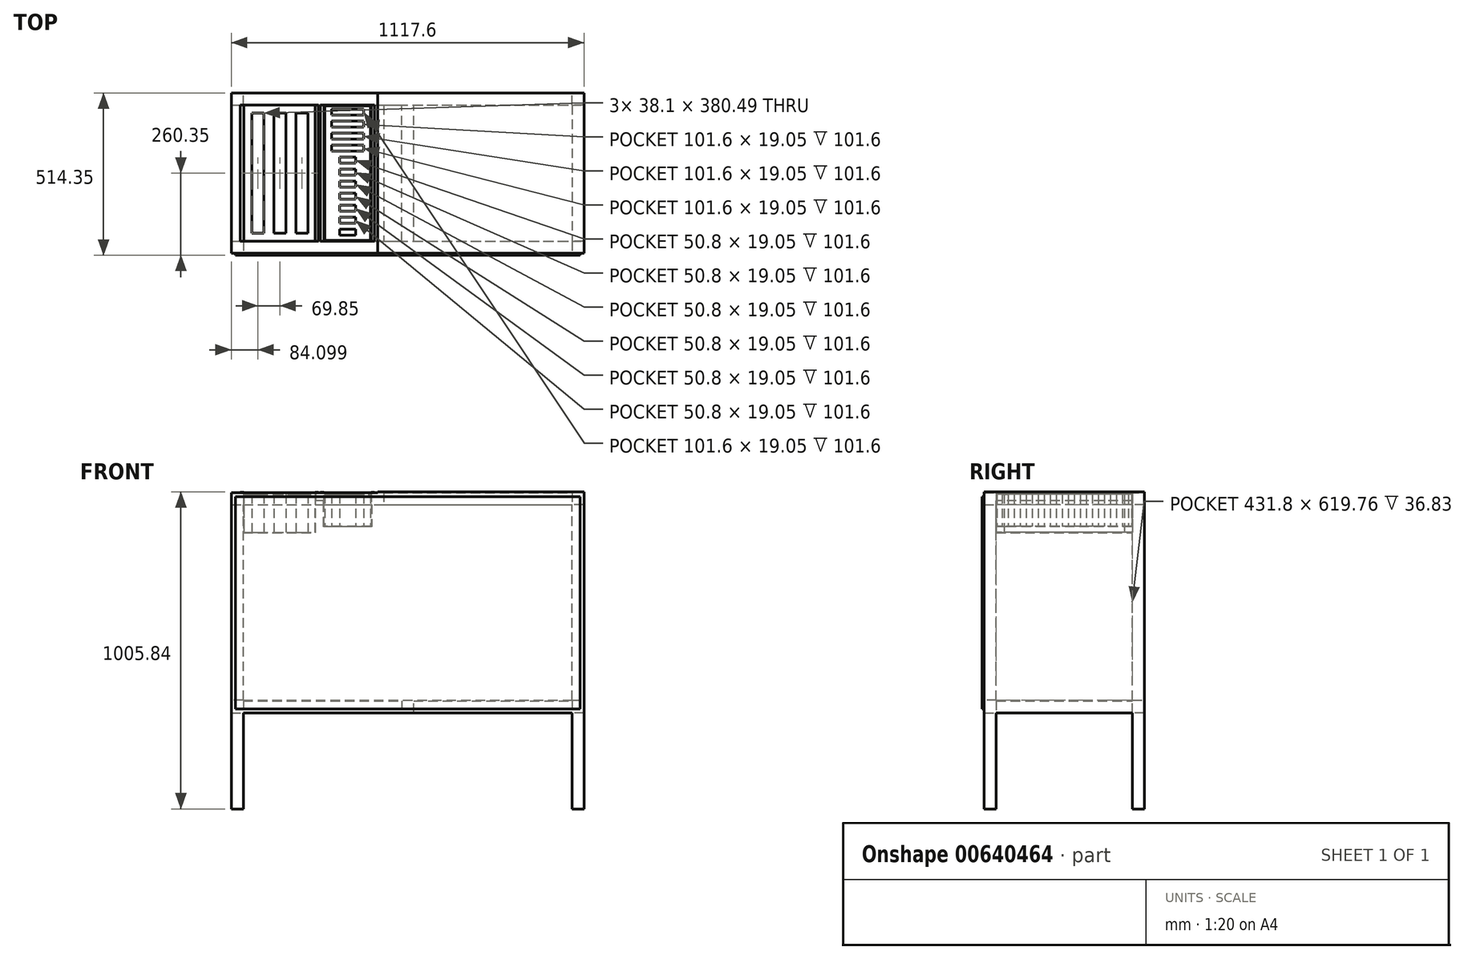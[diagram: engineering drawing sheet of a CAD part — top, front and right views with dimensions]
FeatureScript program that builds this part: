
annotation { "Feature Type Name" : "Feature", "Feature Type Description" : "" }
export const myFeature = defineFeature(function(context is Context, id is Id, definition is map)
    precondition{}
    {
        {
            var Q0;
            Q0=qCreatedBy(makeId("Top.planeOp"),FACE);
            var sketch = newSketch(context, id + "F0", { "sketchPlane" : qUnion([Q0])});
            skLineSegment(sketch, "E0.bottom", {"start": v(-558.8, 254) * mm, "end": v(558.8, 254) * mm});
            skLineSegment(sketch, "E0.top", {"start": v(-558.8, -254) * mm, "end": v(558.8, -254) * mm});
            skLineSegment(sketch, "E0.left", {"start": v(-558.8, 254) * mm, "end": v(-558.8, -254) * mm});
            skLineSegment(sketch, "E0.right", {"start": v(558.8, 254) * mm, "end": v(558.8, -254) * mm});
            skLineSegment(sketch, "E1", {"start": v(-558.8, -254) * mm, "end": v(558.8, 254) * mm, "construction": true});
            skLineSegment(sketch, "E2.0", {"start": v(-520.7, 215.9) * mm, "end": v(-520.7, -215.9) * mm});
            skLineSegment(sketch, "E2.1", {"start": v(-520.7, 215.9) * mm, "end": v(520.7, 215.9) * mm});
            skLineSegment(sketch, "E2.2", {"start": v(520.7, 215.9) * mm, "end": v(520.7, -215.9) * mm});
            skLineSegment(sketch, "E2.3", {"start": v(-520.7, -215.9) * mm, "end": v(520.7, -215.9) * mm});
            skSolve(sketch);
        }
        {
            var Q0;
            Q0 = qSketchRegion(id + "F0", true);
            extrude(context, id + "F1", {"entities" : qUnion([Q0]), "depth" : 38.1 * mm, "offsetDistance" : 25.4 * mm});
        }
        {
            var Q0;
            Q0=makeQuery(id+"F1.opExtrude","CAP_FACE",FACE,{"disambiguationData":[OSD([sQuery(id+"F0.wireOp",EDGE,"E0.bottom"),sQuery(id+"F0.wireOp",EDGE,"E0.top"),sQuery(id+"F0.wireOp",EDGE,"E0.left"),sQuery(id+"F0.wireOp",EDGE,"E0.right"),sQuery(id+"F0.wireOp",EDGE,"E2.0"),sQuery(id+"F0.wireOp",EDGE,"E2.1"),sQuery(id+"F0.wireOp",EDGE,"E2.2"),sQuery(id+"F0.wireOp",EDGE,"E2.3")])],"isStart":true});
            var sketch = newSketch(context, id + "F2", { "sketchPlane" : qUnion([Q0])});
            skLineSegment(sketch, "E3.bottom", {"start": v(-558.8, 254) * mm, "end": v(-520.7, 254) * mm});
            skLineSegment(sketch, "E3.top", {"start": v(-558.8, 215.9) * mm, "end": v(-520.7, 215.9) * mm});
            skLineSegment(sketch, "E3.left", {"start": v(-558.8, 254) * mm, "end": v(-558.8, 215.9) * mm});
            skLineSegment(sketch, "E3.right", {"start": v(-520.7, 254) * mm, "end": v(-520.7, 215.9) * mm});
            skLineSegment(sketch, "E4.bottom", {"start": v(558.8, 254) * mm, "end": v(520.7, 254) * mm});
            skLineSegment(sketch, "E4.top", {"start": v(558.8, 215.9) * mm, "end": v(520.7, 215.9) * mm});
            skLineSegment(sketch, "E4.left", {"start": v(558.8, 254) * mm, "end": v(558.8, 215.9) * mm});
            skLineSegment(sketch, "E4.right", {"start": v(520.7, 254) * mm, "end": v(520.7, 215.9) * mm});
            skLineSegment(sketch, "E5.bottom", {"start": v(558.8, -254) * mm, "end": v(520.7, -254) * mm});
            skLineSegment(sketch, "E5.top", {"start": v(558.8, -215.9) * mm, "end": v(520.7, -215.9) * mm});
            skLineSegment(sketch, "E5.left", {"start": v(558.8, -254) * mm, "end": v(558.8, -215.9) * mm});
            skLineSegment(sketch, "E5.right", {"start": v(520.7, -254) * mm, "end": v(520.7, -215.9) * mm});
            skLineSegment(sketch, "E6.bottom", {"start": v(-558.8, -254) * mm, "end": v(-520.7, -254) * mm});
            skLineSegment(sketch, "E6.top", {"start": v(-558.8, -215.9) * mm, "end": v(-520.7, -215.9) * mm});
            skLineSegment(sketch, "E6.left", {"start": v(-558.8, -254) * mm, "end": v(-558.8, -215.9) * mm});
            skLineSegment(sketch, "E6.right", {"start": v(-520.7, -254) * mm, "end": v(-520.7, -215.9) * mm});
            skSolve(sketch);
        }
        {
            var Q0;
            Q0 = qSketchRegion(id + "F2", true);
            extrude(context, id + "F3", {"entities" : qUnion([Q0]), "operationType" : NewBodyOperationType.ADD, "depth" : 965.2 * mm, "offsetDistance" : 25.4 * mm});
        }
        {
            var Q0;
            Q0=makeQuery(id+"F3.opExtrude","CAP_FACE",FACE,{"disambiguationData":[OSD([sQuery(id+"F2.wireOp",EDGE,"E3.bottom"),sQuery(id+"F2.wireOp",EDGE,"E3.top"),sQuery(id+"F2.wireOp",EDGE,"E3.left"),sQuery(id+"F2.wireOp",EDGE,"E3.right")])],"isStart":false});
            cPlane(context, id + "F4", {"entities" : qUnion([Q0]), "cplaneType" : CPlaneType.OFFSET, "offset" : 304.8 * mm, "oppositeDirection" : true, "width" : 152.4 * mm, "height" : 152.4 * mm});
        }
        {
            var Q0;
            Q0=qCreatedBy(id+"F4.planeOp",FACE);
            var sketch = newSketch(context, id + "F5", { "sketchPlane" : qUnion([Q0])});
            skLineSegment(sketch, "E7.bottom", {"start": v(-558.8, 254) * mm, "end": v(558.8, 254) * mm});
            skLineSegment(sketch, "E7.top", {"start": v(-558.8, -254) * mm, "end": v(558.8, -254) * mm});
            skLineSegment(sketch, "E7.left", {"start": v(-558.8, 254) * mm, "end": v(-558.8, -254) * mm});
            skLineSegment(sketch, "E7.right", {"start": v(558.8, 254) * mm, "end": v(558.8, -254) * mm});
            skLineSegment(sketch, "E8.bottom", {"start": v(-520.7, 215.9) * mm, "end": v(520.7, 215.9) * mm});
            skLineSegment(sketch, "E8.top", {"start": v(-520.7, -215.9) * mm, "end": v(520.7, -215.9) * mm});
            skLineSegment(sketch, "E8.left", {"start": v(-520.7, 215.9) * mm, "end": v(-520.7, -215.9) * mm});
            skLineSegment(sketch, "E8.right", {"start": v(520.7, 215.9) * mm, "end": v(520.7, -215.9) * mm});
            skSolve(sketch);
        }
        {
            var Q0;
            Q0 = qSketchRegion(id + "F5", true);
            extrude(context, id + "F6", {"entities" : qUnion([Q0]), "operationType" : NewBodyOperationType.ADD, "oppositeDirection" : true, "depth" : 38.1 * mm, "offsetDistance" : 25.4 * mm});
        }
        {
            var Q0;
            Q0=makeQuery(id+"F6.boolean.opBoolean","MERGE",FACE,{"derivedFrom":[makeQuery(id+"F3.boolean.opBoolean","MERGE",FACE,{"derivedFrom":[makeQuery(id+"F1.opExtrude","SWEPT_FACE",FACE,{"disambiguationData":[OSD([sQuery(id+"F0.wireOp",EDGE,"E0.left")])]}),makeQuery(id+"F3.opExtrude","SWEPT_FACE",FACE,{"disambiguationData":[OSD([sQuery(id+"F2.wireOp",EDGE,"E3.left")])]}),makeQuery(id+"F3.opExtrude","SWEPT_FACE",FACE,{"disambiguationData":[OSD([sQuery(id+"F2.wireOp",EDGE,"E6.left")])]})]}),makeQuery(id+"F6.opExtrude","SWEPT_FACE",FACE,{"disambiguationData":[OSD([sQuery(id+"F5.wireOp",EDGE,"E7.left")])]})]});
            var sketch = newSketch(context, id + "F7", { "sketchPlane" : qUnion([Q0])});
            skLineSegment(sketch, "E9.0", {"start": v(-215.9, -622.3) * mm, "end": v(-215.9, 0) * mm});
            skLineSegment(sketch, "E10.0", {"start": v(-215.9, 0) * mm, "end": v(215.9, 0) * mm});
            skLineSegment(sketch, "E11.0", {"start": v(215.9, -622.3) * mm, "end": v(215.9, 0) * mm});
            skLineSegment(sketch, "E11.1", {"start": v(215.9, -622.3) * mm, "end": v(-215.9, -622.3) * mm});
            skSolve(sketch);
        }
        {
            var Q0;
            Q0 = qSketchRegion(id + "F7", true);
            extrude(context, id + "F8", {"entities" : qUnion([Q0]), "operationType" : NewBodyOperationType.ADD, "oppositeDirection" : true, "depth" : 1.27 * mm, "offsetDistance" : 25.4 * mm});
        }
        {
            var Q0;
            Q0=makeQuery(id+"F6.boolean.opBoolean","MERGE",FACE,{"derivedFrom":[makeQuery(id+"F3.boolean.opBoolean","MERGE",FACE,{"derivedFrom":[makeQuery(id+"F1.opExtrude","SWEPT_FACE",FACE,{"disambiguationData":[OSD([sQuery(id+"F0.wireOp",EDGE,"E0.right")])]}),makeQuery(id+"F3.opExtrude","SWEPT_FACE",FACE,{"disambiguationData":[OSD([sQuery(id+"F2.wireOp",EDGE,"E4.left")])]}),makeQuery(id+"F3.opExtrude","SWEPT_FACE",FACE,{"disambiguationData":[OSD([sQuery(id+"F2.wireOp",EDGE,"E5.left")])]})]}),makeQuery(id+"F6.opExtrude","SWEPT_FACE",FACE,{"disambiguationData":[OSD([sQuery(id+"F5.wireOp",EDGE,"E7.right")])]})]});
            var sketch = newSketch(context, id + "F9", { "sketchPlane" : qUnion([Q0])});
            skLineSegment(sketch, "E12.0", {"start": v(215.9, 0) * mm, "end": v(-215.9, 0) * mm});
            skLineSegment(sketch, "E12.1", {"start": v(-215.9, -622.3) * mm, "end": v(-215.9, 0) * mm});
            skLineSegment(sketch, "E12.2", {"start": v(215.9, -622.3) * mm, "end": v(215.9, 0) * mm});
            skLineSegment(sketch, "E12.3", {"start": v(-215.9, -622.3) * mm, "end": v(215.9, -622.3) * mm});
            skSolve(sketch);
        }
        {
            var Q0;
            Q0 = qSketchRegion(id + "F9", true);
            extrude(context, id + "F10", {"entities" : qUnion([Q0]), "operationType" : NewBodyOperationType.ADD, "oppositeDirection" : true, "depth" : 1.27 * mm, "offsetDistance" : 25.4 * mm});
        }
        {
            var Q0;
            Q0=makeQuery(id+"F1.opExtrude","SWEPT_FACE",FACE,{"disambiguationData":[OSD([sQuery(id+"F0.wireOp",EDGE,"E2.3")])]});
            var sketch = newSketch(context, id + "F11", { "sketchPlane" : qUnion([Q0])});
            skLineSegment(sketch, "E13.bottom", {"start": v(76.2, 38.1) * mm, "end": v(114.3, 38.1) * mm});
            skLineSegment(sketch, "E13.top", {"start": v(76.2, 0) * mm, "end": v(114.3, 0) * mm});
            skLineSegment(sketch, "E13.left", {"start": v(76.2, 38.1) * mm, "end": v(76.2, 0) * mm});
            skLineSegment(sketch, "E13.right", {"start": v(114.3, 38.1) * mm, "end": v(114.3, 0) * mm});
            skLineSegment(sketch, "E14.bottom", {"start": v(266.7, 38.1) * mm, "end": v(292.1, 38.1) * mm});
            skLineSegment(sketch, "E14.top", {"start": v(266.7, 12.7) * mm, "end": v(292.1, 12.7) * mm});
            skLineSegment(sketch, "E14.left", {"start": v(266.7, 38.1) * mm, "end": v(266.7, 12.7) * mm});
            skLineSegment(sketch, "E14.right", {"start": v(292.1, 38.1) * mm, "end": v(292.1, 12.7) * mm});
            skSolve(sketch);
        }
        {
            var Q0;
            Q0 = qSketchRegion(id + "F11", true);
            var Q1;
            Q1=makeQuery(id+"F1.opExtrude","SWEPT_FACE",FACE,{"disambiguationData":[OSD([sQuery(id+"F0.wireOp",EDGE,"E2.1")])]});
            extrude(context, id + "F12", {"entities" : qUnion([Q0]), "operationType" : NewBodyOperationType.ADD, "endBound" : BoundingType.UP_TO_SURFACE, "depth" : 25.4 * mm, "endBoundEntityFace" : qUnion([Q1]), "offsetDistance" : 25.4 * mm});
        }
        {
            var Q0;
            Q0=makeQuery(id+"F12.boolean.opBoolean","MERGE",FACE,{"derivedFrom":[makeQuery(id+"F1.opExtrude","CAP_FACE",FACE,{"disambiguationData":[OSD([sQuery(id+"F0.wireOp",EDGE,"E0.bottom"),sQuery(id+"F0.wireOp",EDGE,"E0.top"),sQuery(id+"F0.wireOp",EDGE,"E0.left"),sQuery(id+"F0.wireOp",EDGE,"E0.right"),sQuery(id+"F0.wireOp",EDGE,"E2.0"),sQuery(id+"F0.wireOp",EDGE,"E2.1"),sQuery(id+"F0.wireOp",EDGE,"E2.2"),sQuery(id+"F0.wireOp",EDGE,"E2.3")])],"isStart":false}),makeQuery(id+"F12.opExtrude","SWEPT_FACE",FACE,{"disambiguationData":[OSD([sQuery(id+"F11.wireOp",EDGE,"E13.bottom")])]}),makeQuery(id+"F12.opExtrude","SWEPT_FACE",FACE,{"disambiguationData":[OSD([sQuery(id+"F11.wireOp",EDGE,"E14.bottom")])]})]});
            var sketch = newSketch(context, id + "F13", { "sketchPlane" : qUnion([Q0])});
            skLineSegment(sketch, "E15.0", {"start": v(558.8, 254) * mm, "end": v(558.8, -254) * mm});
            skLineSegment(sketch, "E16", {"start": v(558.8, -254) * mm, "end": v(-95.25, -254) * mm});
            skLineSegment(sketch, "E17", {"start": v(-95.25, -254) * mm, "end": v(-95.25, 254) * mm});
            skLineSegment(sketch, "E18", {"start": v(-95.25, 254) * mm, "end": v(558.8, 254) * mm});
            skSolve(sketch);
        }
        {
            var Q0;
            Q0 = qSketchRegion(id + "F13", true);
            extrude(context, id + "F14", {"entities" : qUnion([Q0]), "operationType" : NewBodyOperationType.ADD, "depth" : 2.54 * mm, "offsetDistance" : 25.4 * mm});
        }
        {
            var Q0;
            {var subQ0=sQuery(id+"F0.wireOp",EDGE,"E2.3");var subQ3=sQuery(id+"F0.wireOp",EDGE,"E2.0");Q0=makeQuery(id+"F12.boolean.opBoolean","SPLIT",FACE,{"disambiguationData":[TD([makeQuery(id+"F1.opExtrude","SWEPT_FACE",FACE,{"disambiguationData":[OSD([subQ3])]})])],"derivedFrom":makeQuery(id+"F1.opExtrude","SWEPT_FACE",FACE,{"disambiguationData":[OSD([subQ0])]})});}
            var sketch = newSketch(context, id + "F15", { "sketchPlane" : qUnion([Q0])});
            skLineSegment(sketch, "E19", {"start": v(104.77, 38.1) * mm, "end": v(114.3, 38.1) * mm});
            skLineSegment(sketch, "E20", {"start": v(114.3, 38.1) * mm, "end": v(114.3, -69.85) * mm});
            skLineSegment(sketch, "E21", {"start": v(114.3, -69.85) * mm, "end": v(266.7, -69.85) * mm});
            skLineSegment(sketch, "E22", {"start": v(266.7, -69.85) * mm, "end": v(266.7, 38.1) * mm});
            skLineSegment(sketch, "E23", {"start": v(266.7, 38.1) * mm, "end": v(276.23, 38.1) * mm});
            skLineSegment(sketch, "E24.0", {"start": v(265.43, 39.37) * mm, "end": v(276.23, 39.37) * mm});
            skLineSegment(sketch, "E24.1", {"start": v(104.77, 39.37) * mm, "end": v(115.57, 39.37) * mm});
            skLineSegment(sketch, "E24.2", {"start": v(115.57, 39.37) * mm, "end": v(115.57, -68.58) * mm});
            skLineSegment(sketch, "E24.3", {"start": v(115.57, -68.58) * mm, "end": v(265.43, -68.58) * mm});
            skLineSegment(sketch, "E24.4", {"start": v(265.43, -68.58) * mm, "end": v(265.43, 39.37) * mm});
            skLineSegment(sketch, "E25", {"start": v(104.77, 39.37) * mm, "end": v(104.77, 38.1) * mm});
            skLineSegment(sketch, "E26", {"start": v(276.23, 39.37) * mm, "end": v(276.23, 38.1) * mm});
            skSolve(sketch);
        }
        {
            var Q0;
            Q0 = qSketchRegion(id + "F15", true);
            var Q1;
            {var subQ2=sQuery(id+"F0.wireOp",EDGE,"E2.1");var subQ3=sQuery(id+"F0.wireOp",EDGE,"E2.0");Q1=makeQuery(id+"F12.boolean.opBoolean","SPLIT",FACE,{"disambiguationData":[TD([makeQuery(id+"F1.opExtrude","SWEPT_FACE",FACE,{"disambiguationData":[OSD([subQ3])]})])],"derivedFrom":makeQuery(id+"F1.opExtrude","SWEPT_FACE",FACE,{"disambiguationData":[OSD([subQ2])]})});}
            extrude(context, id + "F16", {"entities" : qUnion([Q0]), "operationType" : NewBodyOperationType.ADD, "endBound" : BoundingType.UP_TO_SURFACE, "depth" : 25.4 * mm, "endBoundEntityFace" : qUnion([Q1]), "offsetDistance" : 25.4 * mm});
        }
        {
            var Q0;
            Q0=makeQuery(id+"F16.opExtrude","SWEPT_FACE",FACE,{"disambiguationData":[OSD([sQuery(id+"F15.wireOp",EDGE,"E24.3")])]});
            var sketch = newSketch(context, id + "F17", { "sketchPlane" : qUnion([Q0])});
            skLineSegment(sketch, "E27.bottom", {"start": v(-241.3, 165.1) * mm, "end": v(-139.7, 165.1) * mm});
            skLineSegment(sketch, "E27.top", {"start": v(-241.3, 146.05) * mm, "end": v(-139.7, 146.05) * mm});
            skLineSegment(sketch, "E27.left", {"start": v(-241.3, 165.1) * mm, "end": v(-241.3, 146.05) * mm});
            skLineSegment(sketch, "E27.right", {"start": v(-139.7, 165.1) * mm, "end": v(-139.7, 146.05) * mm});
            skLineSegment(sketch, "E28.bottom", {"start": v(-241.3, 127) * mm, "end": v(-139.7, 127) * mm});
            skLineSegment(sketch, "E28.top", {"start": v(-241.3, 107.95) * mm, "end": v(-139.7, 107.95) * mm});
            skLineSegment(sketch, "E28.left", {"start": v(-241.3, 127) * mm, "end": v(-241.3, 107.95) * mm});
            skLineSegment(sketch, "E28.right", {"start": v(-139.7, 127) * mm, "end": v(-139.7, 107.95) * mm});
            skLineSegment(sketch, "E29.bottom", {"start": v(-241.3, 88.9) * mm, "end": v(-139.7, 88.9) * mm});
            skLineSegment(sketch, "E29.top", {"start": v(-241.3, 69.85) * mm, "end": v(-139.7, 69.85) * mm});
            skLineSegment(sketch, "E29.left", {"start": v(-241.3, 88.9) * mm, "end": v(-241.3, 69.85) * mm});
            skLineSegment(sketch, "E29.right", {"start": v(-139.7, 88.9) * mm, "end": v(-139.7, 69.85) * mm});
            skLineSegment(sketch, "E30.bottom", {"start": v(-215.9, 50.8) * mm, "end": v(-165.1, 50.8) * mm});
            skLineSegment(sketch, "E30.top", {"start": v(-215.9, 31.75) * mm, "end": v(-165.1, 31.75) * mm});
            skLineSegment(sketch, "E30.left", {"start": v(-215.9, 50.8) * mm, "end": v(-215.9, 31.75) * mm});
            skLineSegment(sketch, "E30.right", {"start": v(-165.1, 50.8) * mm, "end": v(-165.1, 31.75) * mm});
            skLineSegment(sketch, "E31.bottom", {"start": v(-215.9, 12.7) * mm, "end": v(-165.1, 12.7) * mm});
            skLineSegment(sketch, "E31.top", {"start": v(-215.9, -6.35) * mm, "end": v(-165.1, -6.35) * mm});
            skLineSegment(sketch, "E31.left", {"start": v(-215.9, 12.7) * mm, "end": v(-215.9, -6.35) * mm});
            skLineSegment(sketch, "E31.right", {"start": v(-165.1, 12.7) * mm, "end": v(-165.1, -6.35) * mm});
            skLineSegment(sketch, "E32.bottom", {"start": v(-215.9, -25.4) * mm, "end": v(-165.1, -25.4) * mm});
            skLineSegment(sketch, "E32.top", {"start": v(-215.9, -44.45) * mm, "end": v(-165.1, -44.45) * mm});
            skLineSegment(sketch, "E32.left", {"start": v(-215.9, -25.4) * mm, "end": v(-215.9, -44.45) * mm});
            skLineSegment(sketch, "E32.right", {"start": v(-165.1, -25.4) * mm, "end": v(-165.1, -44.45) * mm});
            skLineSegment(sketch, "E33.bottom", {"start": v(-215.9, -63.5) * mm, "end": v(-165.1, -63.5) * mm});
            skLineSegment(sketch, "E33.top", {"start": v(-215.9, -82.55) * mm, "end": v(-165.1, -82.55) * mm});
            skLineSegment(sketch, "E33.left", {"start": v(-215.9, -63.5) * mm, "end": v(-215.9, -82.55) * mm});
            skLineSegment(sketch, "E33.right", {"start": v(-165.1, -63.5) * mm, "end": v(-165.1, -82.55) * mm});
            skLineSegment(sketch, "E34.bottom", {"start": v(-215.9, -101.6) * mm, "end": v(-165.1, -101.6) * mm});
            skLineSegment(sketch, "E34.top", {"start": v(-215.9, -120.65) * mm, "end": v(-165.1, -120.65) * mm});
            skLineSegment(sketch, "E34.left", {"start": v(-215.9, -101.6) * mm, "end": v(-215.9, -120.65) * mm});
            skLineSegment(sketch, "E34.right", {"start": v(-165.1, -101.6) * mm, "end": v(-165.1, -120.65) * mm});
            skLineSegment(sketch, "E35.bottom", {"start": v(-215.9, -139.7) * mm, "end": v(-165.1, -139.7) * mm});
            skLineSegment(sketch, "E35.top", {"start": v(-215.9, -158.75) * mm, "end": v(-165.1, -158.75) * mm});
            skLineSegment(sketch, "E35.left", {"start": v(-215.9, -139.7) * mm, "end": v(-215.9, -158.75) * mm});
            skLineSegment(sketch, "E35.right", {"start": v(-165.1, -139.7) * mm, "end": v(-165.1, -158.75) * mm});
            skLineSegment(sketch, "E36.bottom", {"start": v(-215.9, -196.85) * mm, "end": v(-165.1, -196.85) * mm});
            skLineSegment(sketch, "E36.top", {"start": v(-215.9, -177.8) * mm, "end": v(-165.1, -177.8) * mm});
            skLineSegment(sketch, "E36.left", {"start": v(-215.9, -196.85) * mm, "end": v(-215.9, -177.8) * mm});
            skLineSegment(sketch, "E36.right", {"start": v(-165.1, -196.85) * mm, "end": v(-165.1, -177.8) * mm});
            skLineSegment(sketch, "E37.bottom", {"start": v(-241.3, 203.2) * mm, "end": v(-139.7, 203.2) * mm});
            skLineSegment(sketch, "E37.top", {"start": v(-241.3, 184.15) * mm, "end": v(-139.7, 184.15) * mm});
            skLineSegment(sketch, "E37.left", {"start": v(-241.3, 203.2) * mm, "end": v(-241.3, 184.15) * mm});
            skLineSegment(sketch, "E37.right", {"start": v(-139.7, 203.2) * mm, "end": v(-139.7, 184.15) * mm});
            skLineSegment(sketch, "E38", {"start": v(-190.5, -215.9) * mm, "end": v(-190.5, 215.9) * mm, "construction": true});
            skLineSegment(sketch, "E39.0", {"start": v(-262.9, 213.36) * mm, "end": v(-118.1, 213.36) * mm});
            skLineSegment(sketch, "E39.1", {"start": v(-262.9, 213.36) * mm, "end": v(-262.9, -213.36) * mm});
            skLineSegment(sketch, "E39.2", {"start": v(-262.9, -213.36) * mm, "end": v(-118.1, -213.36) * mm});
            skLineSegment(sketch, "E39.3", {"start": v(-118.1, 213.36) * mm, "end": v(-118.1, -213.36) * mm});
            skSolve(sketch);
        }
        {
            var Q0;
            Q0 = qSketchRegion(id + "F17", true);
            extrude(context, id + "F18", {"entities" : qUnion([Q0]), "operationType" : NewBodyOperationType.ADD, "depth" : 101.6 * mm, "offsetDistance" : 25.4 * mm});
        }
        {
            var Q0;
            {var subQ0=sQuery(id+"F5.wireOp",EDGE,"E8.top");var subQ1=sQuery(id+"F5.wireOp",EDGE,"E8.right");var subQ2=sQuery(id+"F5.wireOp",EDGE,"E8.left");var subQ3=sQuery(id+"F5.wireOp",EDGE,"E7.top");var subQ4=makeQuery(id+"F6.opExtrude","CAP_FACE",FACE,{"disambiguationData":[OSD([sQuery(id+"F5.wireOp",EDGE,"E7.bottom"),subQ3,sQuery(id+"F5.wireOp",EDGE,"E7.left"),sQuery(id+"F5.wireOp",EDGE,"E7.right"),sQuery(id+"F5.wireOp",EDGE,"E8.bottom"),subQ0,subQ2,subQ1])],"isStart":false});Q0=makeQuery(id+"F6.boolean.opBoolean","SPLIT",FACE,{"disambiguationData":[TD([makeQuery(id+"F1.opExtrude","SWEPT_FACE",FACE,{"disambiguationData":[OSD([sQuery(id+"F0.wireOp",EDGE,"E0.bottom")])]})])],"derivedFrom":subQ4});}
            var sketch = newSketch(context, id + "F19", { "sketchPlane" : qUnion([Q0])});
            skLineSegment(sketch, "E40.bottom", {"start": v(-558.8, 254) * mm, "end": v(558.8, 254) * mm});
            skLineSegment(sketch, "E40.top", {"start": v(-558.8, -254) * mm, "end": v(558.8, -254) * mm});
            skLineSegment(sketch, "E40.left", {"start": v(-558.8, 254) * mm, "end": v(-558.8, -254) * mm});
            skLineSegment(sketch, "E40.right", {"start": v(558.8, 254) * mm, "end": v(558.8, -254) * mm});
            skSolve(sketch);
        }
        {
            var Q0;
            Q0 = qSketchRegion(id + "F19", true);
            extrude(context, id + "F20", {"entities" : qUnion([Q0]), "operationType" : NewBodyOperationType.ADD, "depth" : 2.54 * mm, "offsetDistance" : 25.4 * mm});
        }
        {
            var Q0;
            Q0=makeQuery(id+"F6.opExtrude","SWEPT_FACE",FACE,{"disambiguationData":[OSD([sQuery(id+"F5.wireOp",EDGE,"E8.top")])]});
            var sketch = newSketch(context, id + "F21", { "sketchPlane" : qUnion([Q0])});
            skLineSegment(sketch, "E41.bottom", {"start": v(-19.05, -660.4) * mm, "end": v(19.05, -660.4) * mm});
            skLineSegment(sketch, "E41.top", {"start": v(-19.05, -622.3) * mm, "end": v(19.05, -622.3) * mm});
            skLineSegment(sketch, "E41.left", {"start": v(-19.05, -660.4) * mm, "end": v(-19.05, -622.3) * mm});
            skLineSegment(sketch, "E41.right", {"start": v(19.05, -660.4) * mm, "end": v(19.05, -622.3) * mm});
            skSolve(sketch);
        }
        {
            var Q0;
            Q0 = qSketchRegion(id + "F21", true);
            var Q1;
            Q1=makeQuery(id+"F6.opExtrude","SWEPT_FACE",FACE,{"disambiguationData":[OSD([sQuery(id+"F5.wireOp",EDGE,"E8.bottom")])]});
            extrude(context, id + "F22", {"entities" : qUnion([Q0]), "operationType" : NewBodyOperationType.ADD, "endBound" : BoundingType.UP_TO_SURFACE, "depth" : 25.4 * mm, "endBoundEntityFace" : qUnion([Q1]), "offsetDistance" : 25.4 * mm});
        }
        {
            var Q0;
            Q0=makeQuery(id+"F20.boolean.opBoolean","MERGE",FACE,{"derivedFrom":[makeQuery(id+"F14.boolean.opBoolean","MERGE",FACE,{"derivedFrom":[makeQuery(id+"F6.boolean.opBoolean","MERGE",FACE,{"derivedFrom":[makeQuery(id+"F3.boolean.opBoolean","MERGE",FACE,{"derivedFrom":[makeQuery(id+"F1.opExtrude","SWEPT_FACE",FACE,{"disambiguationData":[OSD([sQuery(id+"F0.wireOp",EDGE,"E0.top")])]}),makeQuery(id+"F3.opExtrude","SWEPT_FACE",FACE,{"disambiguationData":[OSD([sQuery(id+"F2.wireOp",EDGE,"E3.bottom")])]}),makeQuery(id+"F3.opExtrude","SWEPT_FACE",FACE,{"disambiguationData":[OSD([sQuery(id+"F2.wireOp",EDGE,"E4.bottom")])]})]}),makeQuery(id+"F6.opExtrude","SWEPT_FACE",FACE,{"disambiguationData":[OSD([sQuery(id+"F5.wireOp",EDGE,"E7.bottom")])]})]}),makeQuery(id+"F14.opExtrude","SWEPT_FACE",FACE,{"disambiguationData":[OSD([sQuery(id+"F13.wireOp",EDGE,"E16")])]})]}),makeQuery(id+"F20.opExtrude","SWEPT_FACE",FACE,{"disambiguationData":[OSD([sQuery(id+"F19.wireOp",EDGE,"E40.top")])]})]});
            var sketch = newSketch(context, id + "F23", { "sketchPlane" : qUnion([Q0])});
            skLineSegment(sketch, "E42.bottom", {"start": v(-546.1, 25.4) * mm, "end": v(546.1, 25.4) * mm});
            skLineSegment(sketch, "E42.top", {"start": v(-546.1, -647.7) * mm, "end": v(546.1, -647.7) * mm});
            skLineSegment(sketch, "E42.left", {"start": v(-546.1, 25.4) * mm, "end": v(-546.1, -647.7) * mm});
            skLineSegment(sketch, "E42.right", {"start": v(546.1, 25.4) * mm, "end": v(546.1, -647.7) * mm});
            skSolve(sketch);
        }
        {
            var Q0;
            Q0 = qSketchRegion(id + "F23", true);
            extrude(context, id + "F24", {"entities" : qUnion([Q0]), "operationType" : NewBodyOperationType.ADD, "depth" : 6.35 * mm, "offsetDistance" : 25.4 * mm});
        }
        {
            var Q0;
            {var subQ4=sQuery(id+"F0.wireOp",EDGE,"E2.1");var subQ5=sQuery(id+"F0.wireOp",EDGE,"E2.0");var subQ15=makeQuery(id+"F1.opExtrude","SWEPT_FACE",FACE,{"disambiguationData":[OSD([subQ5])]});Q0=makeQuery(id+"F16.boolean.opBoolean","SPLIT",FACE,{"disambiguationData":[TD([subQ15])],"derivedFrom":makeQuery(id+"F12.boolean.opBoolean","SPLIT",FACE,{"disambiguationData":[TD([subQ15])],"derivedFrom":makeQuery(id+"F1.opExtrude","SWEPT_FACE",FACE,{"disambiguationData":[OSD([subQ4])]})})});}
            var sketch = newSketch(context, id + "F25", { "sketchPlane" : qUnion([Q0])});
            skSolve(sketch);
        }
        {
            var Q0;
            {var subQ0=sQuery(id+"F0.wireOp",EDGE,"E2.0");var subQ2=sQuery(id+"F0.wireOp",EDGE,"E2.1");Q0=makeQuery(id+"F25.imprint","IMPRINT",FACE,{"disambiguationData":[TD([[makeQuery(id+"F25.imprint","IMPRINT",EDGE,{"derivedFrom":makeQuery(id+"F1.opExtrude","SWEPT_EDGE",EDGE,{"disambiguationData":[OSD([subQ0,subQ2])]})}),1.0]])]});}
            var sketch = newSketch(context, id + "F26", { "sketchPlane" : qUnion([Q0])});
            skLineSegment(sketch, "E43", {"start": v(-530.2, 38.13) * mm, "end": v(-520.67, 38.13) * mm});
            skLineSegment(sketch, "E44", {"start": v(-520.67, 38.13) * mm, "end": v(-520.67, -88.87) * mm});
            skLineSegment(sketch, "E45", {"start": v(-520.67, -88.87) * mm, "end": v(-292.13, -88.87) * mm});
            skLineSegment(sketch, "E46", {"start": v(-292.13, -88.87) * mm, "end": v(-292.13, 38.13) * mm});
            skLineSegment(sketch, "E47", {"start": v(-292.13, 38.13) * mm, "end": v(-282.6, 38.13) * mm});
            skLineSegment(sketch, "E48.0", {"start": v(-293.4, 39.4) * mm, "end": v(-282.6, 39.4) * mm});
            skLineSegment(sketch, "E48.1", {"start": v(-530.2, 39.4) * mm, "end": v(-519.4, 39.4) * mm});
            skLineSegment(sketch, "E48.2", {"start": v(-519.4, 39.4) * mm, "end": v(-519.4, -87.6) * mm});
            skLineSegment(sketch, "E48.3", {"start": v(-519.4, -87.6) * mm, "end": v(-293.4, -87.6) * mm});
            skLineSegment(sketch, "E48.4", {"start": v(-293.4, -87.6) * mm, "end": v(-293.4, 39.4) * mm});
            skLineSegment(sketch, "E49", {"start": v(-282.6, 39.4) * mm, "end": v(-282.6, 38.13) * mm});
            skLineSegment(sketch, "E50", {"start": v(-530.2, 39.4) * mm, "end": v(-530.2, 38.13) * mm});
            skSolve(sketch);
        }
        {
            var Q0;
            Q0 = qSketchRegion(id + "F26", true);
            var Q1;
            {var subQ2=sQuery(id+"F0.wireOp",EDGE,"E2.3");var subQ5=sQuery(id+"F0.wireOp",EDGE,"E2.0");var subQ15=makeQuery(id+"F1.opExtrude","SWEPT_FACE",FACE,{"disambiguationData":[OSD([subQ5])]});Q1=makeQuery(id+"F16.boolean.opBoolean","SPLIT",FACE,{"disambiguationData":[TD([subQ15])],"derivedFrom":makeQuery(id+"F12.boolean.opBoolean","SPLIT",FACE,{"disambiguationData":[TD([subQ15])],"derivedFrom":makeQuery(id+"F1.opExtrude","SWEPT_FACE",FACE,{"disambiguationData":[OSD([subQ2])]})})});}
            extrude(context, id + "F27", {"entities" : qUnion([Q0]), "operationType" : NewBodyOperationType.ADD, "endBound" : BoundingType.UP_TO_SURFACE, "depth" : 25.4 * mm, "endBoundEntityFace" : qUnion([Q1]), "offsetDistance" : 25.4 * mm});
        }
        {
            var Q0;
            Q0=makeQuery(id+"F27.opExtrude","SWEPT_FACE",FACE,{"disambiguationData":[OSD([sQuery(id+"F26.wireOp",EDGE,"E48.3")])]});
            cPlane(context, id + "F28", {"entities" : qUnion([Q0]), "cplaneType" : CPlaneType.OFFSET, "offset" : 0.03 * mm, "width" : 152.4 * mm, "height" : 152.4 * mm});
        }
        {
            var Q0;
            Q0=qCreatedBy(id+"F28.planeOp",FACE);
            var sketch = newSketch(context, id + "F29", { "sketchPlane" : qUnion([Q0])});
            skLineSegment(sketch, "E51.bottom", {"start": v(-519.15, 215.65) * mm, "end": v(-293.65, 215.65) * mm});
            skLineSegment(sketch, "E51.top", {"start": v(-519.15, -215.65) * mm, "end": v(-293.65, -215.65) * mm});
            skLineSegment(sketch, "E51.left", {"start": v(-519.15, 215.65) * mm, "end": v(-519.15, -215.65) * mm});
            skLineSegment(sketch, "E51.right", {"start": v(-293.65, 215.65) * mm, "end": v(-293.65, -215.65) * mm});
            skLineSegment(sketch, "E52.bottom", {"start": v(-493.75, 190.25) * mm, "end": v(-455.65, 190.25) * mm});
            skLineSegment(sketch, "E52.top", {"start": v(-493.75, -190.25) * mm, "end": v(-455.65, -190.25) * mm});
            skLineSegment(sketch, "E52.left", {"start": v(-493.75, 190.25) * mm, "end": v(-493.75, -190.25) * mm});
            skLineSegment(sketch, "E52.right", {"start": v(-455.65, 190.25) * mm, "end": v(-455.65, -190.25) * mm});
            skPoint(sketch, "E53.firstSnap0", {"position": v(-474.7, 190.25) * mm});
            skLineSegment(sketch, "E53.bottom", {"start": v(-354.05, 190.25) * mm, "end": v(-315.95, 190.25) * mm});
            skLineSegment(sketch, "E53.top", {"start": v(-354.05, -190.25) * mm, "end": v(-315.95, -190.25) * mm});
            skLineSegment(sketch, "E53.left", {"start": v(-354.05, 190.25) * mm, "end": v(-354.05, -190.25) * mm});
            skLineSegment(sketch, "E53.right", {"start": v(-315.95, 190.25) * mm, "end": v(-315.95, -190.25) * mm});
            skLineSegment(sketch, "E54.bottom", {"start": v(-423.9, 190.25) * mm, "end": v(-385.8, 190.25) * mm});
            skLineSegment(sketch, "E54.top", {"start": v(-423.9, -190.25) * mm, "end": v(-385.8, -190.25) * mm});
            skLineSegment(sketch, "E54.left", {"start": v(-423.9, 190.25) * mm, "end": v(-423.9, -190.25) * mm});
            skLineSegment(sketch, "E54.right", {"start": v(-385.8, 190.25) * mm, "end": v(-385.8, -190.25) * mm});
            skSolve(sketch);
        }
        {
            var Q0;
            Q0 = qSketchRegion(id + "F29", true);
            var Q1;
            Q1=makeQuery(id+"F18.opExtrude","CAP_FACE",FACE,{"disambiguationData":[OSD([sQuery(id+"F17.wireOp",EDGE,"E27.bottom"),sQuery(id+"F17.wireOp",EDGE,"E27.top"),sQuery(id+"F17.wireOp",EDGE,"E27.left"),sQuery(id+"F17.wireOp",EDGE,"E27.right"),sQuery(id+"F17.wireOp",EDGE,"E28.bottom"),sQuery(id+"F17.wireOp",EDGE,"E28.top"),sQuery(id+"F17.wireOp",EDGE,"E28.left"),sQuery(id+"F17.wireOp",EDGE,"E28.right"),sQuery(id+"F17.wireOp",EDGE,"E29.bottom"),sQuery(id+"F17.wireOp",EDGE,"E29.top"),sQuery(id+"F17.wireOp",EDGE,"E29.left"),sQuery(id+"F17.wireOp",EDGE,"E29.right"),sQuery(id+"F17.wireOp",EDGE,"E30.bottom"),sQuery(id+"F17.wireOp",EDGE,"E30.top"),sQuery(id+"F17.wireOp",EDGE,"E30.left"),sQuery(id+"F17.wireOp",EDGE,"E30.right"),sQuery(id+"F17.wireOp",EDGE,"E31.bottom"),sQuery(id+"F17.wireOp",EDGE,"E31.top"),sQuery(id+"F17.wireOp",EDGE,"E31.left"),sQuery(id+"F17.wireOp",EDGE,"E31.right"),sQuery(id+"F17.wireOp",EDGE,"E32.bottom"),sQuery(id+"F17.wireOp",EDGE,"E32.top"),sQuery(id+"F17.wireOp",EDGE,"E32.left"),sQuery(id+"F17.wireOp",EDGE,"E32.right"),sQuery(id+"F17.wireOp",EDGE,"E33.bottom"),sQuery(id+"F17.wireOp",EDGE,"E33.top"),sQuery(id+"F17.wireOp",EDGE,"E33.left"),sQuery(id+"F17.wireOp",EDGE,"E33.right"),sQuery(id+"F17.wireOp",EDGE,"E34.bottom"),sQuery(id+"F17.wireOp",EDGE,"E34.top"),sQuery(id+"F17.wireOp",EDGE,"E34.left"),sQuery(id+"F17.wireOp",EDGE,"E34.right"),sQuery(id+"F17.wireOp",EDGE,"E35.bottom"),sQuery(id+"F17.wireOp",EDGE,"E35.top"),sQuery(id+"F17.wireOp",EDGE,"E35.left"),sQuery(id+"F17.wireOp",EDGE,"E35.right"),sQuery(id+"F17.wireOp",EDGE,"E36.bottom"),sQuery(id+"F17.wireOp",EDGE,"E36.top"),sQuery(id+"F17.wireOp",EDGE,"E36.left"),sQuery(id+"F17.wireOp",EDGE,"E36.right"),sQuery(id+"F17.wireOp",EDGE,"E37.bottom"),sQuery(id+"F17.wireOp",EDGE,"E37.top"),sQuery(id+"F17.wireOp",EDGE,"E37.left"),sQuery(id+"F17.wireOp",EDGE,"E37.right"),sQuery(id+"F17.wireOp",EDGE,"E39.0"),sQuery(id+"F17.wireOp",EDGE,"E39.1"),sQuery(id+"F17.wireOp",EDGE,"E39.2"),sQuery(id+"F17.wireOp",EDGE,"E39.3")])],"isStart":false});
            extrude(context, id + "F30", {"entities" : qUnion([Q0]), "endBound" : BoundingType.UP_TO_SURFACE, "depth" : 127 * mm, "endBoundEntityFace" : qUnion([Q1]), "offsetDistance" : 25.4 * mm});
        }
    });
